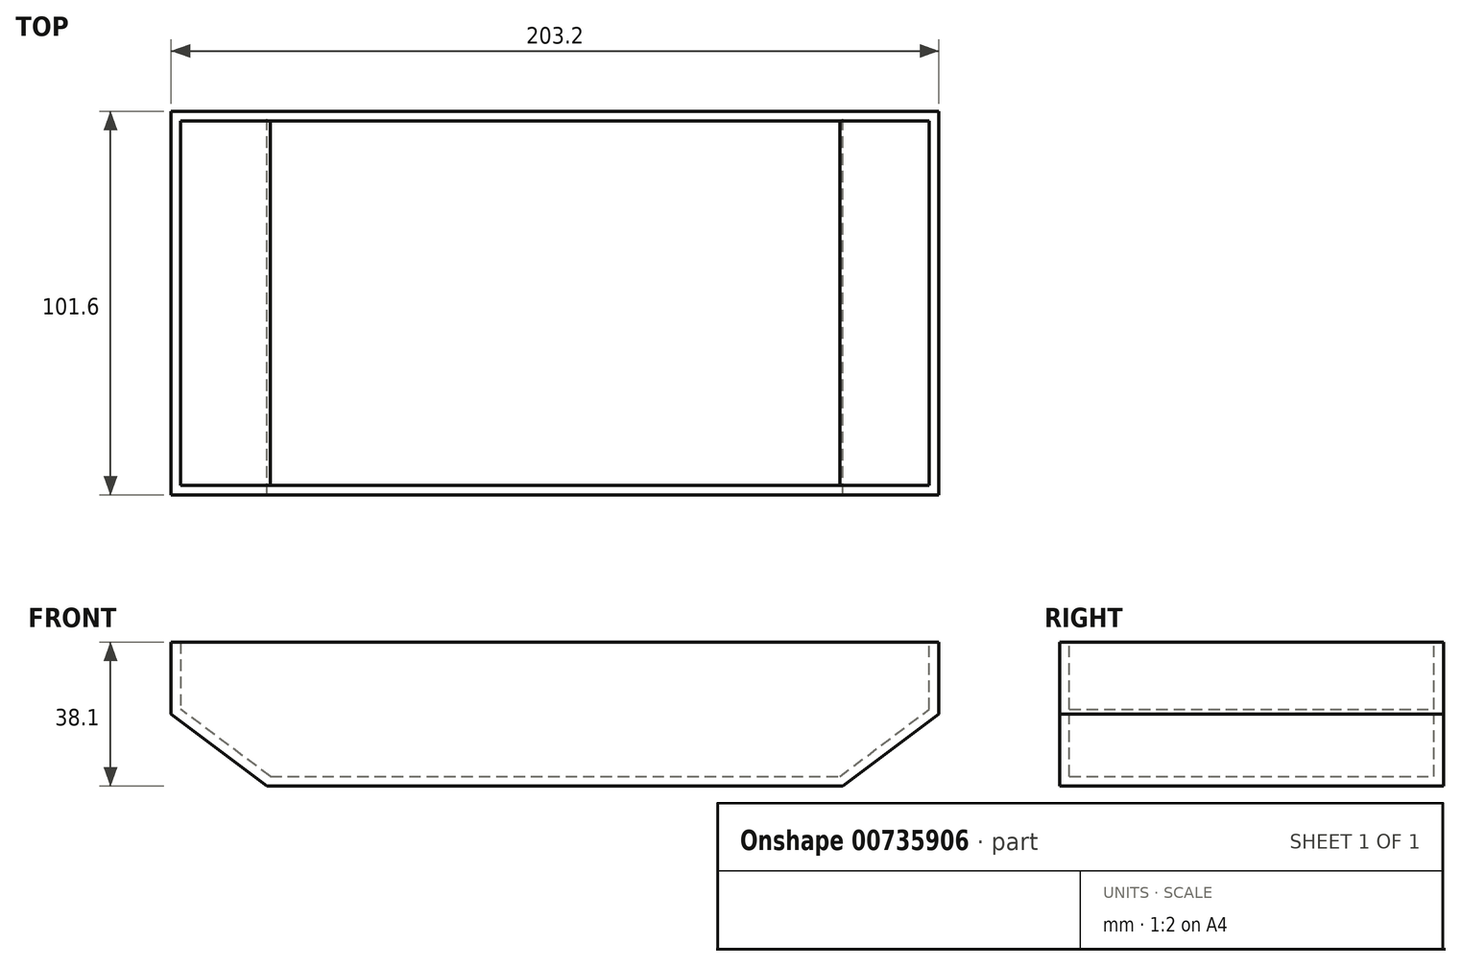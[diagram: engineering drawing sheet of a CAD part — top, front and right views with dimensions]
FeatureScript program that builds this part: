
annotation { "Feature Type Name" : "Feature", "Feature Type Description" : "" }
export const myFeature = defineFeature(function(context is Context, id is Id, definition is map)
    precondition{}
    {
        {
            var Q0;
            Q0=qCreatedBy(makeId("Front.planeOp"),FACE);
            var sketch = newSketch(context, id + "F0", { "sketchPlane" : qUnion([Q0])});
            skLineSegment(sketch, "E0", {"start": v(-152.4, -48.32) * mm, "end": v(0, -48.32) * mm});
            skLineSegment(sketch, "E1", {"start": v(0, -48.32) * mm, "end": v(0, -29.27) * mm});
            skLineSegment(sketch, "E2", {"start": v(0, -29.27) * mm, "end": v(25.4, -29.27) * mm});
            skLineSegment(sketch, "E3", {"start": v(25.4, -29.27) * mm, "end": v(25.4, -10.22) * mm});
            skLineSegment(sketch, "E4", {"start": v(25.4, -10.22) * mm, "end": v(-177.8, -10.22) * mm});
            skLineSegment(sketch, "E5", {"start": v(-177.8, -10.22) * mm, "end": v(-177.8, -29.27) * mm});
            skLineSegment(sketch, "E6", {"start": v(-177.8, -29.27) * mm, "end": v(-152.4, -29.27) * mm});
            skLineSegment(sketch, "E7", {"start": v(-152.4, -29.27) * mm, "end": v(-152.4, -48.32) * mm});
            skLineSegment(sketch, "E8", {"start": v(-152.4, -48.32) * mm, "end": v(-177.8, -29.27) * mm});
            skLineSegment(sketch, "E9", {"start": v(0, -48.32) * mm, "end": v(25.4, -29.27) * mm});
            skLineSegment(sketch, "E10", {"start": v(-152.4, -48.32) * mm, "end": v(-152.4, -48.32) * mm});
            skSolve(sketch);
        }
        {
            var Q0;
            Q0=makeQuery(id+"F0.imprint","IMPRINT",FACE,{"disambiguationData":[TD([[makeQuery(id+"F0.imprint","IMPRINT",EDGE,{"derivedFrom":sQuery(id+"F0.wireOp",EDGE,"E1")}),-1.0]])]});
            var Q1;
            Q1=makeQuery(id+"F0.imprint","IMPRINT",FACE,{"disambiguationData":[TD([[makeQuery(id+"F0.imprint","IMPRINT",EDGE,{"derivedFrom":sQuery(id+"F0.wireOp",EDGE,"E6")}),-1.0]])]});
            var Q2;
            Q2=makeQuery(id+"F0.imprint","IMPRINT",FACE,{"disambiguationData":[TD([[makeQuery(id+"F0.imprint","IMPRINT",EDGE,{"derivedFrom":sQuery(id+"F0.wireOp",EDGE,"E0")}),1.0]])]});
            extrude(context, id + "F1", {"entities" : qUnion([Q0, Q1, Q2]), "depth" : 101.6 * mm, "offsetDistance" : 25.4 * mm});
        }
        {
            var Q0;
            Q0=makeQuery(id+"F1.opExtrude","SWEPT_FACE",FACE,{"disambiguationData":[OSD([sQuery(id+"F0.wireOp",EDGE,"E4")])]});
            shell(context, id + "F2", {"entities" : qUnion([Q0]), "thickness" : 2.54 * mm});
        }
    });
